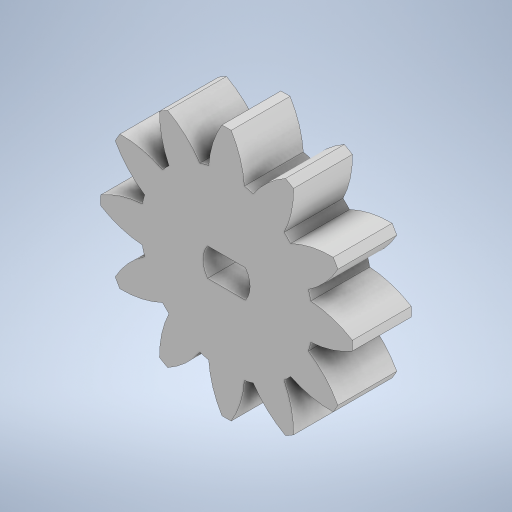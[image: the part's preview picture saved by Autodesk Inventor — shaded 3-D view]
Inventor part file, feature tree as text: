
AUTODESK INVENTOR PART (.ipt)
format: ipt  version: 2023.1 (Build 271208000, 208)  size: 329,728 bytes
history: native  units: mm
features: extrude x4, sketch x2, pattern_circular x1, projected_geometry x1
ambient origin geometry x8: Origin, YZ Plane, XZ Plane, XY Plane, X Axis, Y Axis, Z Axis, Center Point
bodies: Body1 (feature_tree)
feature tree (8):
  sketch  "스케치1"
  extrude  "돌출2"  Depth=24.0mm
  extrude  "돌출3"  Depth=28.0mm
  extrude  "돌출4"  Depth=19.0mm
  extrude  "돌출5"  Depth=1.57mm
  pattern_circular  "원형 패턴1"  [2 undecoded]
  sketch  "스케치2"
  projected_geometry  "투영된 루프1"
note: 2 required parameter values undecoded (feature->parameter linkage not recoverable at this tier; creation-order binding heuristic only, values carry confidence <= 0.55)
